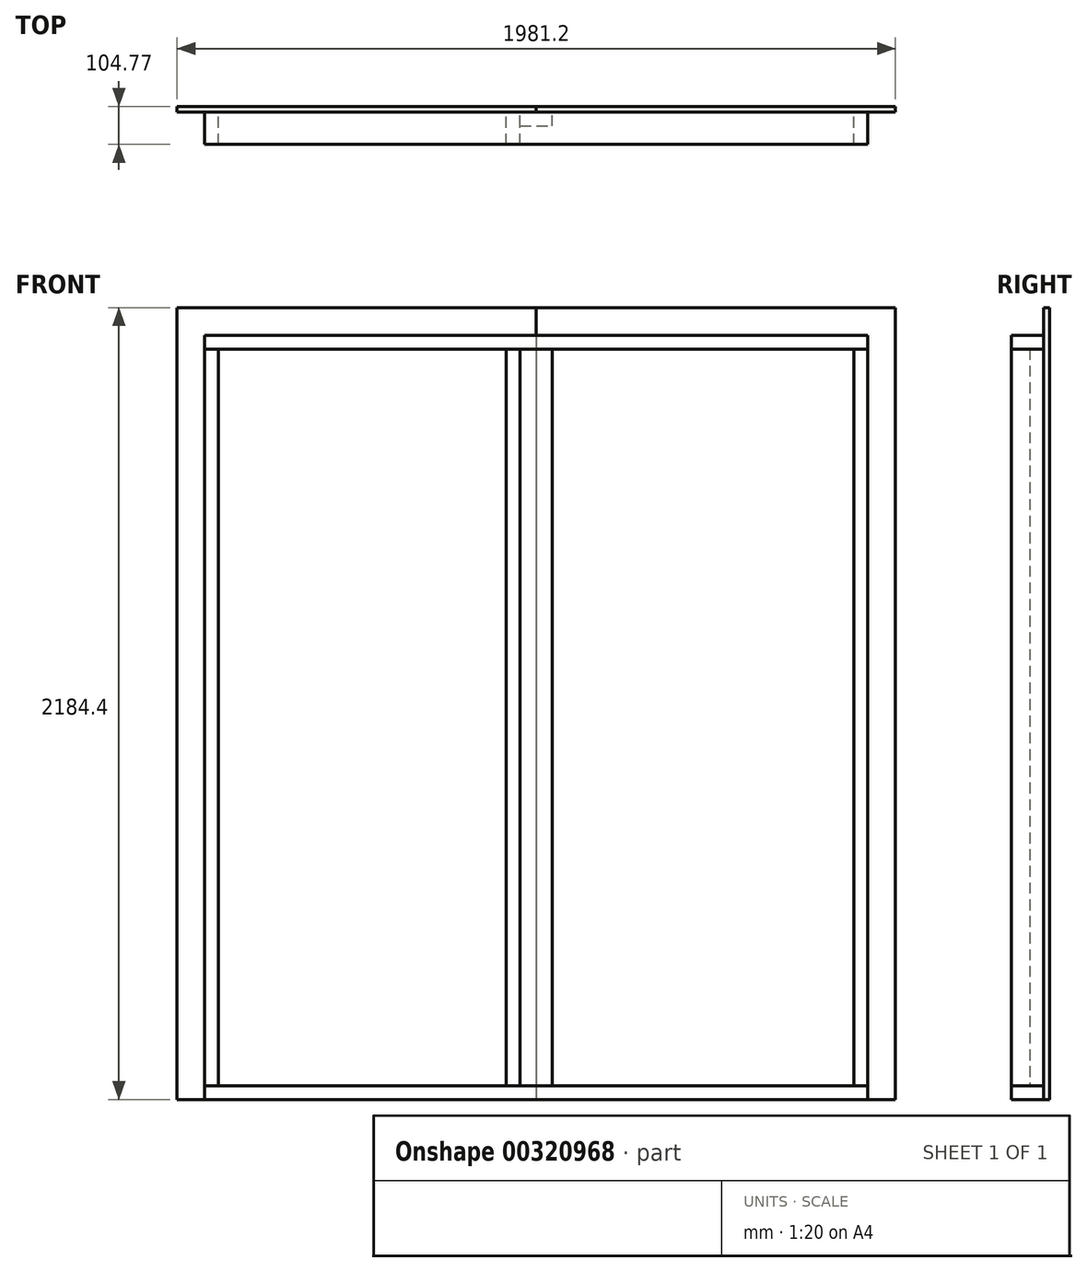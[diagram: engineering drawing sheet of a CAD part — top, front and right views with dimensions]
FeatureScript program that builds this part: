
annotation { "Feature Type Name" : "Feature", "Feature Type Description" : "" }
export const myFeature = defineFeature(function(context is Context, id is Id, definition is map)
    precondition{}
    {
        {
            var Q0;
            Q0=qCreatedBy(makeId("Front.planeOp"),FACE);
            var sketch = newSketch(context, id + "F0", { "sketchPlane" : qUnion([Q0])});
            skLineSegment(sketch, "E0.bottom", {"start": v(0, 0) * mm, "end": v(1981.2, 0) * mm});
            skLineSegment(sketch, "E0.top", {"start": v(0, 2184.4) * mm, "end": v(1981.2, 2184.4) * mm});
            skLineSegment(sketch, "E0.left", {"start": v(0, 0) * mm, "end": v(0, 2184.4) * mm});
            skLineSegment(sketch, "E0.right", {"start": v(1981.2, 0) * mm, "end": v(1981.2, 2184.4) * mm});
            skLineSegment(sketch, "E1", {"start": v(990.6, 2184.4) * mm, "end": v(990.6, 0) * mm});
            skSolve(sketch);
        }
        {
            var Q0;
            {var subQ0=sQuery(id+"F0.wireOp",EDGE,"E0.left");Q0=makeQuery(id+"F0.imprint","IMPRINT",FACE,{"disambiguationData":[TD([[makeQuery(id+"F0.imprint","IMPRINT",EDGE,{"derivedFrom":subQ0}),-1.0]])]});}
            extrude(context, id + "F1", {"entities" : qUnion([Q0]), "depth" : 15.88 * mm});
        }
        {
            var Q0;
            {var subQ0=sQuery(id+"F0.wireOp",EDGE,"E0.right");Q0=makeQuery(id+"F0.imprint","IMPRINT",FACE,{"disambiguationData":[TD([[makeQuery(id+"F0.imprint","IMPRINT",EDGE,{"derivedFrom":subQ0}),1.0]])]});}
            extrude(context, id + "F2", {"entities" : qUnion([Q0]), "depth" : 15.88 * mm});
        }
        {
            var Q0;
            Q0=makeQuery(id+"F1.opExtrude","CAP_FACE",FACE,{"disambiguationData":[OSD([sQuery(id+"F0.wireOp",EDGE,"E0.bottom"),sQuery(id+"F0.wireOp",EDGE,"E0.top"),sQuery(id+"F0.wireOp",EDGE,"E0.left"),sQuery(id+"F0.wireOp",EDGE,"E1")])],"isStart":false});
            var sketch = newSketch(context, id + "F3", { "sketchPlane" : qUnion([Q0])});
            skLineSegment(sketch, "E2.bottom", {"start": v(76.2, 0) * mm, "end": v(1905, 0) * mm});
            skLineSegment(sketch, "E2.top", {"start": v(76.2, 2108.2) * mm, "end": v(1905, 2108.2) * mm});
            skLineSegment(sketch, "E2.left", {"start": v(76.2, 0) * mm, "end": v(76.2, 2108.2) * mm});
            skLineSegment(sketch, "E2.right", {"start": v(1905, 0) * mm, "end": v(1905, 2108.2) * mm});
            skLineSegment(sketch, "E3", {"start": v(990.6, 2108.2) * mm, "end": v(990.6, 2184.4) * mm, "construction": true});
            skLineSegment(sketch, "E4", {"start": v(76.2, 38.1) * mm, "end": v(114.3, 38.1) * mm});
            skLineSegment(sketch, "E5", {"start": v(1866.9, 2070.1) * mm, "end": v(1866.9, 38.1) * mm});
            skLineSegment(sketch, "E6", {"start": v(1905, 2070.1) * mm, "end": v(1866.9, 2070.1) * mm});
            skLineSegment(sketch, "E7", {"start": v(114.3, 2070.1) * mm, "end": v(114.3, 38.1) * mm});
            skLineSegment(sketch, "E8.bottom", {"start": v(946.15, 2070.1) * mm, "end": v(1035.05, 2070.1) * mm});
            skLineSegment(sketch, "E8.top", {"start": v(946.15, 38.1) * mm, "end": v(1035.05, 38.1) * mm});
            skLineSegment(sketch, "E8.left", {"start": v(946.15, 2070.1) * mm, "end": v(946.15, 38.1) * mm});
            skLineSegment(sketch, "E8.right", {"start": v(1035.05, 2070.1) * mm, "end": v(1035.05, 38.1) * mm});
            skLineSegment(sketch, "E9", {"start": v(990.6, 2070.1) * mm, "end": v(990.6, 2108.2) * mm, "construction": true});
            skLineSegment(sketch, "E10", {"start": v(114.3, 38.1) * mm, "end": v(946.15, 38.1) * mm});
            skLineSegment(sketch, "E11", {"start": v(1866.9, 38.1) * mm, "end": v(1905, 38.1) * mm});
            skLineSegment(sketch, "E12", {"start": v(1035.05, 38.1) * mm, "end": v(1866.9, 38.1) * mm});
            skLineSegment(sketch, "E13", {"start": v(946.15, 2070.1) * mm, "end": v(114.3, 2070.1) * mm});
            skLineSegment(sketch, "E14", {"start": v(1035.05, 2070.1) * mm, "end": v(946.15, 2070.1) * mm});
            skLineSegment(sketch, "E15", {"start": v(114.3, 2070.1) * mm, "end": v(76.2, 2070.1) * mm});
            skLineSegment(sketch, "E16", {"start": v(1866.9, 2070.1) * mm, "end": v(1035.05, 2070.1) * mm});
            skLineSegment(sketch, "E17", {"start": v(908.05, 38.1) * mm, "end": v(908.05, 2070.1) * mm});
            skSolve(sketch);
        }
        {
            var Q0;
            {var subQ4=sQuery(id+"F3.wireOp",EDGE,"E6");Q0=makeQuery(id+"F3.imprint","IMPRINT",FACE,{"disambiguationData":[TD([[makeQuery(id+"F3.imprint","IMPRINT",EDGE,{"derivedFrom":subQ4}),-1.0]])]});}
            var Q1;
            {var subQ1=sQuery(id+"F3.wireOp",EDGE,"E13");Q1=makeQuery(id+"F3.imprint","IMPRINT",FACE,{"disambiguationData":[TD([[makeQuery(id+"F3.imprint","IMPRINT",EDGE,{"derivedFrom":subQ1}),-1.0]])]});}
            var Q2;
            {var subQ4=sQuery(id+"F3.wireOp",EDGE,"E11");Q2=makeQuery(id+"F3.imprint","IMPRINT",FACE,{"disambiguationData":[TD([[makeQuery(id+"F3.imprint","IMPRINT",EDGE,{"derivedFrom":subQ4}),-1.0]])]});}
            var Q3;
            {var subQ4=sQuery(id+"F3.wireOp",EDGE,"E4");Q3=makeQuery(id+"F3.imprint","IMPRINT",FACE,{"disambiguationData":[TD([[makeQuery(id+"F3.imprint","IMPRINT",EDGE,{"derivedFrom":subQ4}),-1.0]])]});}
            extrude(context, id + "F4", {"entities" : qUnion([Q0, Q1, Q2, Q3]), "depth" : 88.9 * mm});
        }
        {
            var Q0;
            {var subQ0=sQuery(id+"F3.wireOp",EDGE,"E4");Q0=makeQuery(id+"F3.imprint","IMPRINT",FACE,{"disambiguationData":[TD([[makeQuery(id+"F3.imprint","IMPRINT",EDGE,{"derivedFrom":subQ0}),1.0]])]});}
            var Q1;
            Q1=makeQuery(id+"F3.imprint","IMPRINT",FACE,{"disambiguationData":[TD([[makeQuery(id+"F3.imprint","IMPRINT",EDGE,{"derivedFrom":sQuery(id+"F3.wireOp",EDGE,"E5")}),1.0]])]});
            var Q2;
            {var subQ0=sQuery(id+"F3.wireOp",EDGE,"E8.left");Q2=makeQuery(id+"F3.imprint","IMPRINT",FACE,{"disambiguationData":[TD([[makeQuery(id+"F3.imprint","IMPRINT",EDGE,{"derivedFrom":subQ0}),-1.0]])]});}
            extrude(context, id + "F5", {"entities" : qUnion([Q0, Q1, Q2]), "depth" : 88.9 * mm});
        }
        {
            var Q0;
            {var subQ0=sQuery(id+"F3.wireOp",EDGE,"E8.left");Q0=makeQuery(id+"F3.imprint","IMPRINT",FACE,{"disambiguationData":[TD([[makeQuery(id+"F3.imprint","IMPRINT",EDGE,{"derivedFrom":subQ0}),1.0]])]});}
            var Q1;
            {var subQ0=sQuery(id+"F3.wireOp",EDGE,"E8.right");Q1=makeQuery(id+"F3.imprint","IMPRINT",FACE,{"disambiguationData":[TD([[makeQuery(id+"F3.imprint","IMPRINT",EDGE,{"derivedFrom":subQ0}),-1.0]])]});}
            extrude(context, id + "F6", {"entities" : qUnion([Q0, Q1]), "depth" : 38.1 * mm});
        }
    });
